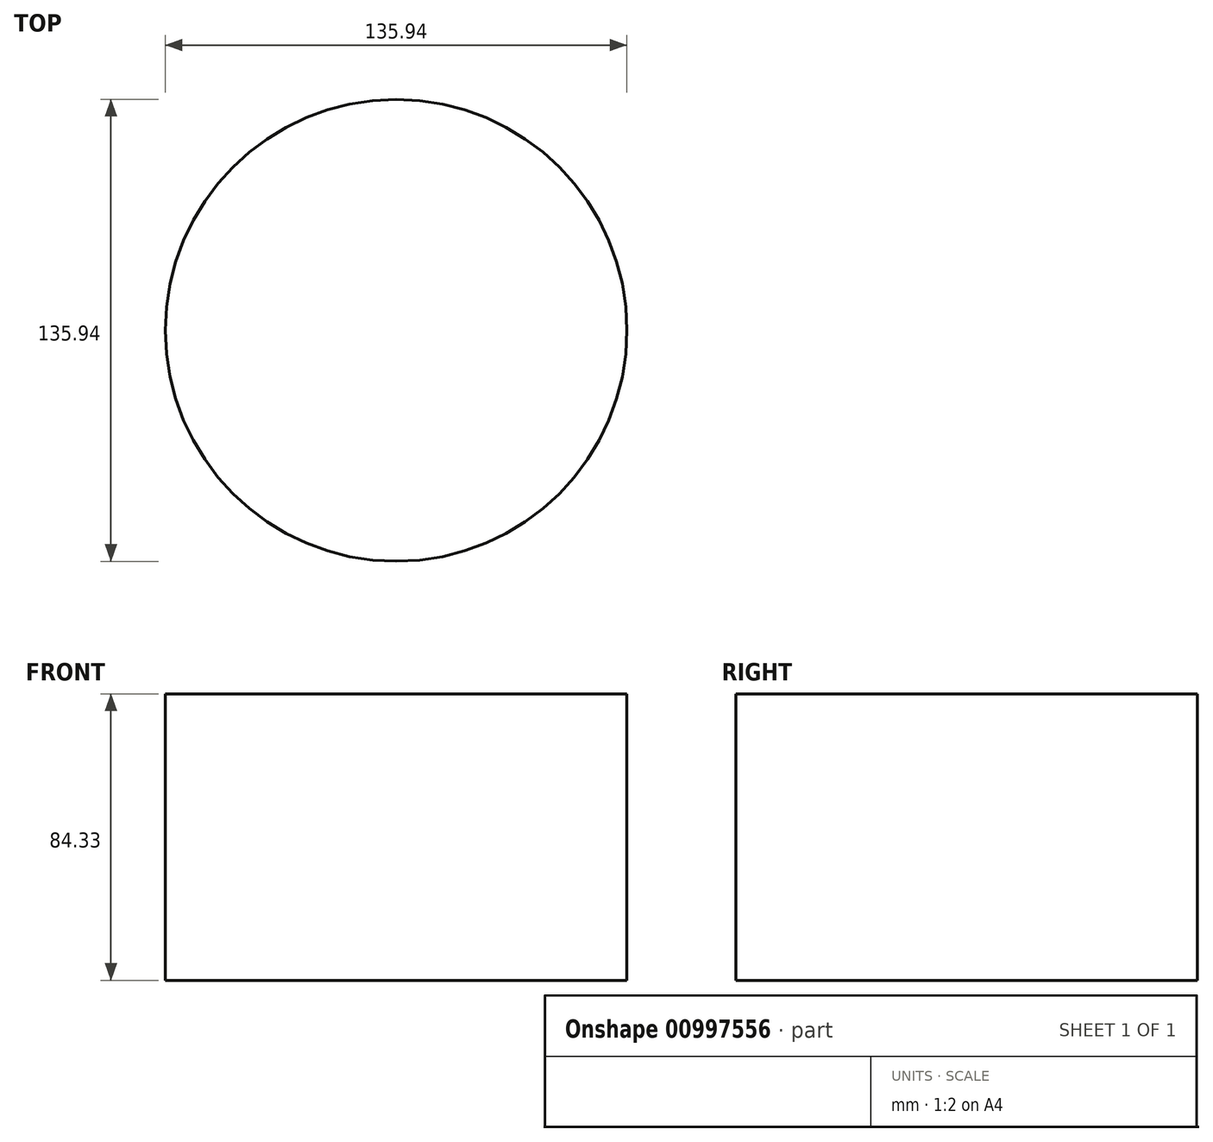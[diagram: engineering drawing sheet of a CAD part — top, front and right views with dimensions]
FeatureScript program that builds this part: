
annotation { "Feature Type Name" : "Feature", "Feature Type Description" : "" }
export const myFeature = defineFeature(function(context is Context, id is Id, definition is map)
    precondition{}
    {
        {
            var Q0;
            Q0=qCreatedBy(makeId("Top.planeOp"),FACE);
            var sketch = newSketch(context, id + "F0", { "sketchPlane" : qUnion([Q0])});
            skCircle(sketch, "E0", {"center": v(0, 0) * mm, "radius": 67.97 * mm});
            skSolve(sketch);
        }
        {
            var Q0;
            Q0 = qSketchRegion(id + "F0", true);
            extrude(context, id + "F1", {"entities" : qUnion([Q0]), "depth" : 58.93 * mm, "offsetDistance" : 25.4 * mm});
        }
        {
            var Q0;
            Q0=qCreatedBy(makeId("Top.planeOp"),FACE);
            var sketch = newSketch(context, id + "F2", { "sketchPlane" : qUnion([Q0])});
            skCircle(sketch, "E1.cCircle", {"center": v(-0.87, 0.97) * mm, "radius": 48.02 * mm, "construction": true});
            skLineSegment(sketch, "E1.0", {"start": v(23.5, -40.4) * mm, "end": v(-24.52, -40.82) * mm});
            skLineSegment(sketch, "E1.1", {"start": v(-24.52, -40.82) * mm, "end": v(-48.89, 0.55) * mm});
            skLineSegment(sketch, "E1.2", {"start": v(-48.89, 0.55) * mm, "end": v(-25.24, 42.34) * mm});
            skLineSegment(sketch, "E1.3", {"start": v(-25.24, 42.34) * mm, "end": v(22.78, 42.76) * mm});
            skLineSegment(sketch, "E1.4", {"start": v(22.78, 42.76) * mm, "end": v(47.14, 1.38) * mm});
            skLineSegment(sketch, "E1.5", {"start": v(47.14, 1.38) * mm, "end": v(23.5, -40.4) * mm});
            skSolve(sketch);
        }
        {
            var Q0;
            Q0=makeQuery(id+"F2.imprint","IMPRINT",FACE,{"disambiguationData":[TD([[makeQuery(id+"F2.imprint","IMPRINT",EDGE,{"derivedFrom":sQuery(id+"F2.wireOp",EDGE,"E1.0")}),-1.0]])]});
            var Q1;
            Q1=makeQuery(id+"F1.opExtrude","CAP_FACE",FACE,{"disambiguationData":[OSD([sQuery(id+"F0.wireOp",EDGE,"E0")])],"isStart":false});
            var Q2;
            Q2=makeQuery(id+"F1.opExtrude","CAP_FACE",FACE,{"disambiguationData":[OSD([sQuery(id+"F0.wireOp",EDGE,"E0")])],"isStart":true});
            extrude(context, id + "F3", {"entities" : qUnion([Q0, Q1, Q2]), "operationType" : NewBodyOperationType.ADD, "depth" : 25.4 * mm, "offsetDistance" : 25.4 * mm});
        }
    });
